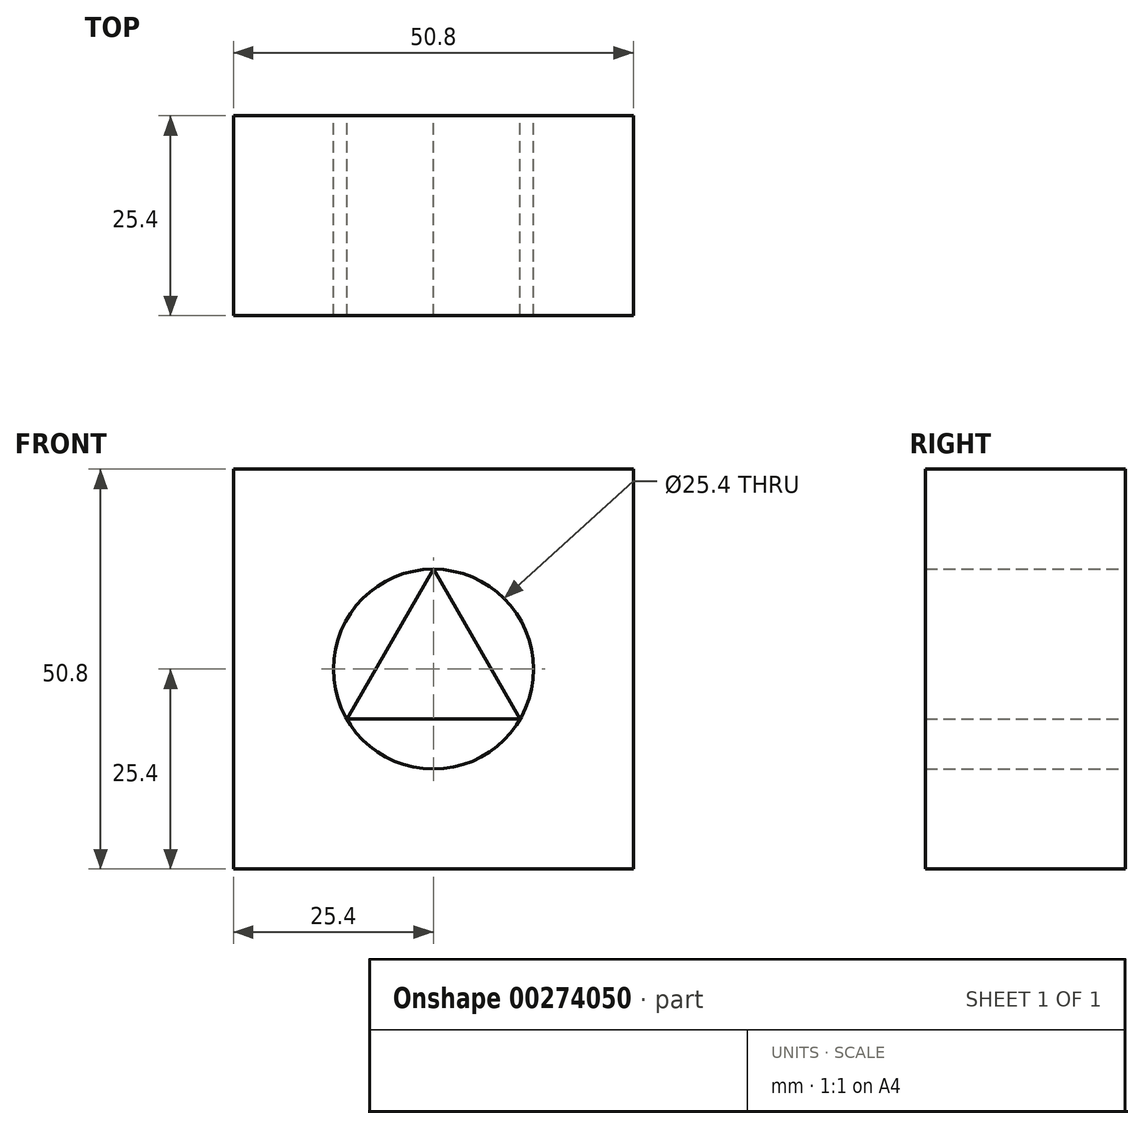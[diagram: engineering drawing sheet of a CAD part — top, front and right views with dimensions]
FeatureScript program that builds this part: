
annotation { "Feature Type Name" : "Feature", "Feature Type Description" : "" }
export const myFeature = defineFeature(function(context is Context, id is Id, definition is map)
    precondition{}
    {
        {
            var Q0;
            Q0=qCreatedBy(makeId("Front.planeOp"),FACE);
            var sketch = newSketch(context, id + "F0", { "sketchPlane" : qUnion([Q0])});
            skLineSegment(sketch, "E0.bottom", {"start": v(0, 0) * mm, "end": v(50.8, 0) * mm});
            skLineSegment(sketch, "E0.top", {"start": v(0, 50.8) * mm, "end": v(50.8, 50.8) * mm});
            skLineSegment(sketch, "E0.left", {"start": v(0, 0) * mm, "end": v(0, 50.8) * mm});
            skLineSegment(sketch, "E0.right", {"start": v(50.8, 0) * mm, "end": v(50.8, 50.8) * mm});
            skPoint(sketch, "E1.centerSnap0", {"position": v(25.4, 50.8) * mm});
            skPoint(sketch, "E1.centerSnap1", {"position": v(50.8, 25.4) * mm});
            skLineSegment(sketch, "E2.0", {"start": v(25.4, 38.1) * mm, "end": v(36.4, 19.05) * mm});
            skLineSegment(sketch, "E2.1", {"start": v(36.4, 19.05) * mm, "end": v(14.4, 19.05) * mm});
            skLineSegment(sketch, "E2.2", {"start": v(14.4, 19.05) * mm, "end": v(25.4, 38.1) * mm});
            skCircle(sketch, "E3", {"center": v(25.4, 25.4) * mm, "radius": 12.7 * mm});
            skSolve(sketch);
        }
        {
            var Q0;
            Q0=makeQuery(id+"F0.imprint","IMPRINT",FACE,{"disambiguationData":[TD([[makeQuery(id+"F0.imprint","IMPRINT",EDGE,{"derivedFrom":sQuery(id+"F0.wireOp",EDGE,"E0.bottom")}),1.0]])]});
            var Q1;
            Q1=makeQuery(id+"F0.imprint","IMPRINT",FACE,{"disambiguationData":[TD([[makeQuery(id+"F0.imprint","IMPRINT",EDGE,{"derivedFrom":sQuery(id+"F0.wireOp",EDGE,"E2.0")}),-1.0]])]});
            extrude(context, id + "F1", {"entities" : qUnion([Q0, Q1]), "depth" : 25.4 * mm});
        }
    });
